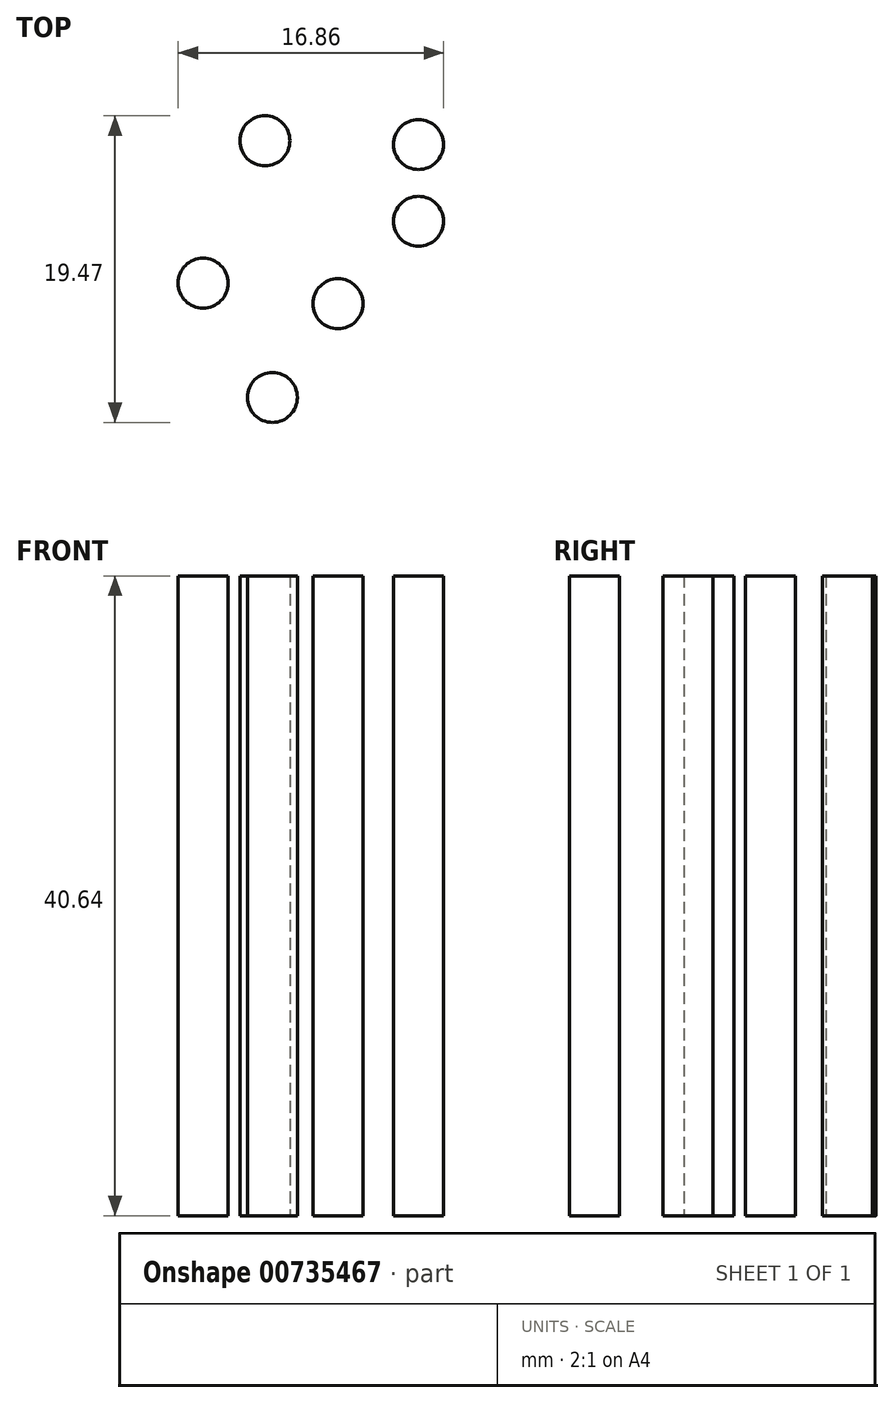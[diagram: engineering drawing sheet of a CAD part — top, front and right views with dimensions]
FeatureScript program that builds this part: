
annotation { "Feature Type Name" : "Feature", "Feature Type Description" : "" }
export const myFeature = defineFeature(function(context is Context, id is Id, definition is map)
    precondition{}
    {
        {
            var Q0;
            Q0=qCreatedBy(makeId("Top.planeOp"),FACE);
            var sketch = newSketch(context, id + "F0", { "sketchPlane" : qUnion([Q0])});
            skCircle(sketch, "E0", {"center": v(-71.35, 41.26) * mm, "radius": 1.59 * mm});
            skCircle(sketch, "E1", {"center": v(-61.6, 41.02) * mm, "radius": 1.59 * mm});
            skCircle(sketch, "E2", {"center": v(-61.6, 36.14) * mm, "radius": 1.59 * mm});
            skCircle(sketch, "E3", {"center": v(-75.28, 32.21) * mm, "radius": 1.59 * mm});
            skCircle(sketch, "E4", {"center": v(-66.7, 30.9) * mm, "radius": 1.59 * mm});
            skCircle(sketch, "E5", {"center": v(-70.87, 24.95) * mm, "radius": 1.59 * mm});
            skSolve(sketch);
        }
        {
            var Q0;
            Q0 = qSketchRegion(id + "F0", true);
            extrude(context, id + "F1", {"entities" : qUnion([Q0]), "depth" : 40.64 * mm, "offsetDistance" : 25.4 * mm});
        }
    });
